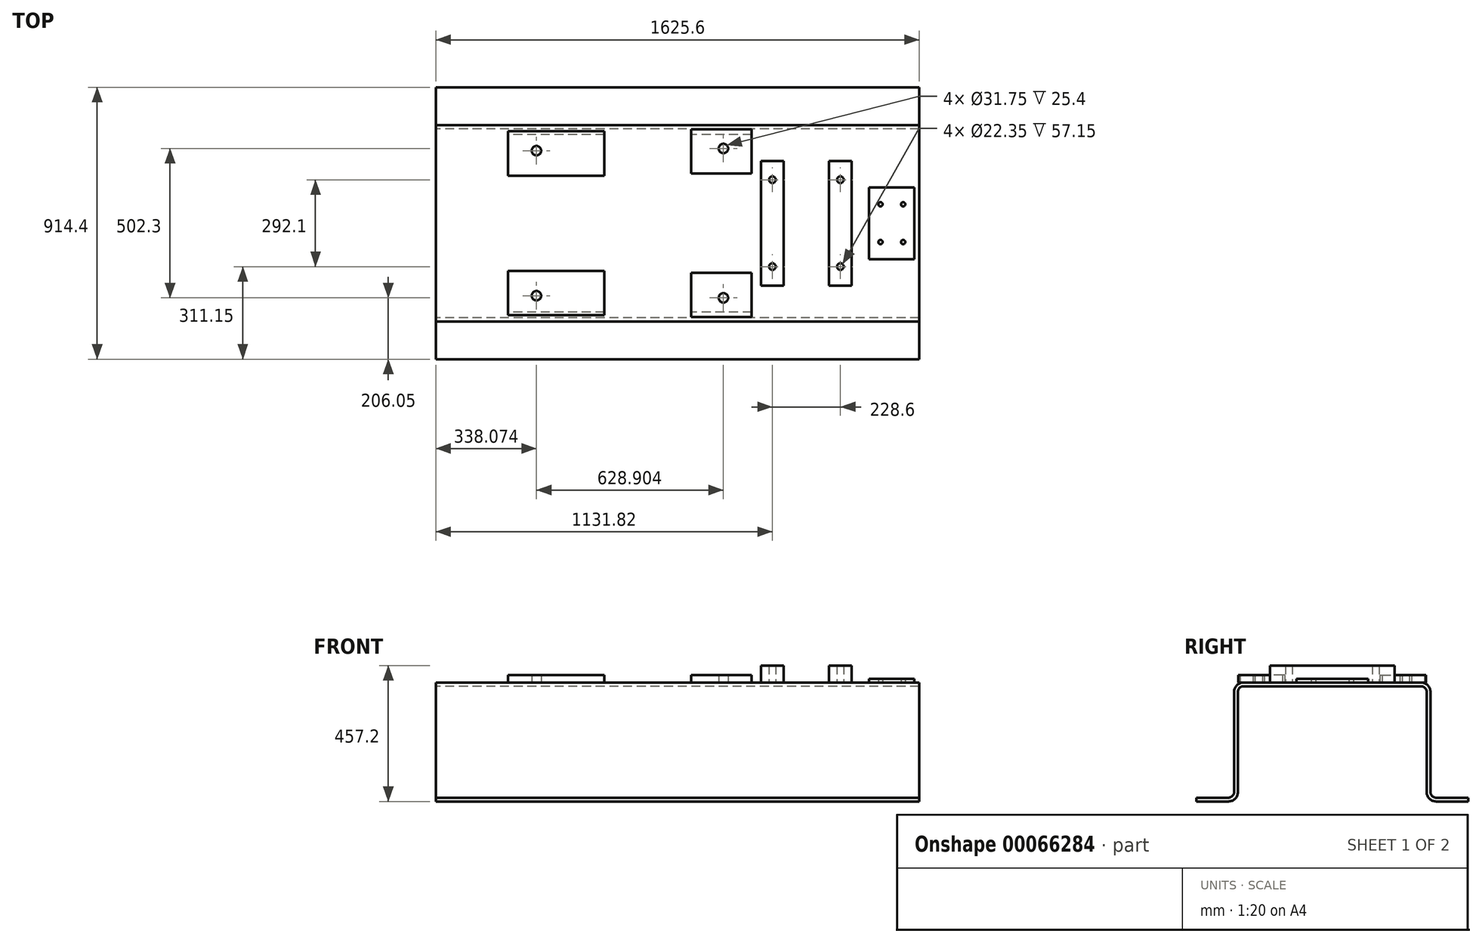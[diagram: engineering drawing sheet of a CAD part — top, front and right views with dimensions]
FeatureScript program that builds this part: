
annotation { "Feature Type Name" : "Feature", "Feature Type Description" : "" }
export const myFeature = defineFeature(function(context is Context, id is Id, definition is map)
    precondition{}
    {
        {
            var Q0;
            Q0=qCreatedBy(makeId("Right.planeOp"),FACE);
            var sketch = newSketch(context, id + "F0", { "sketchPlane" : qUnion([Q0])});
            skLineSegment(sketch, "E0", {"start": v(349.25, 0) * mm, "end": v(457.2, 0) * mm});
            skLineSegment(sketch, "E1.0", {"start": v(349.25, 12.7) * mm, "end": v(457.2, 12.7) * mm});
            skLineSegment(sketch, "E2.0", {"start": v(0, 400.05) * mm, "end": v(298.45, 400.05) * mm});
            skLineSegment(sketch, "E3", {"start": v(0, -167.8) * mm, "end": v(0, 400.05) * mm, "construction": true});
            skLineSegment(sketch, "E4.0", {"start": v(0, 387.35) * mm, "end": v(298.45, 387.35) * mm});
            skLineSegment(sketch, "E5.0", {"start": v(330.2, 31.75) * mm, "end": v(330.2, 368.3) * mm});
            skLineSegment(sketch, "E6.0", {"start": v(317.5, 31.75) * mm, "end": v(317.5, 368.3) * mm});
            skArc(sketch, "E7.filletArc", {"start": v(330.2, 31.75) * mm, "mid": v(335.78, 18.28) * mm, "end": v(349.25, 12.7) * mm});
            skArc(sketch, "E8.filletArc", {"start": v(317.5, 368.3) * mm, "mid": v(311.92, 381.77) * mm, "end": v(298.45, 387.35) * mm});
            skArc(sketch, "E9.filletArc", {"start": v(330.2, 368.3) * mm, "mid": v(320.9, 390.75) * mm, "end": v(298.45, 400.05) * mm});
            skPoint(sketch, "E10.newPointA", {"position": v(-457.2, 0) * mm});
            skArc(sketch, "E10.filletArc", {"start": v(317.5, 31.75) * mm, "mid": v(326.8, 9.3) * mm, "end": v(349.25, 0) * mm});
            skLineSegment(sketch, "E11", {"start": v(457.2, 12.7) * mm, "end": v(457.2, 0) * mm});
            skLineSegment(sketch, "E12.MirrorCS", {"start": v(-457.2, 12.7) * mm, "end": v(-457.2, 0) * mm});
            skArc(sketch, "E13.MirrorCS", {"start": v(-330.2, 368.3) * mm, "mid": v(-320.9, 390.75) * mm, "end": v(-298.45, 400.05) * mm});
            skArc(sketch, "E14.MirrorCS", {"start": v(-330.2, 31.75) * mm, "mid": v(-335.78, 18.28) * mm, "end": v(-349.25, 12.7) * mm});
            skArc(sketch, "E15.MirrorCS", {"start": v(-317.5, 368.3) * mm, "mid": v(-311.92, 381.77) * mm, "end": v(-298.45, 387.35) * mm});
            skArc(sketch, "E16.MirrorCS", {"start": v(-317.5, 31.75) * mm, "mid": v(-326.8, 9.3) * mm, "end": v(-349.25, 0) * mm});
            skLineSegment(sketch, "E17.MirrorCS", {"start": v(-349.25, 0) * mm, "end": v(-457.2, 0) * mm});
            skLineSegment(sketch, "E18.MirrorCS", {"start": v(-349.25, 12.7) * mm, "end": v(-457.2, 12.7) * mm});
            skLineSegment(sketch, "E19.MirrorCS", {"start": v(0, 400.05) * mm, "end": v(-298.45, 400.05) * mm});
            skLineSegment(sketch, "E20.MirrorCS", {"start": v(0, 387.35) * mm, "end": v(-298.45, 387.35) * mm});
            skLineSegment(sketch, "E21.MirrorCS", {"start": v(-317.5, 31.75) * mm, "end": v(-317.5, 368.3) * mm});
            skLineSegment(sketch, "E22.MirrorCS", {"start": v(-330.2, 31.75) * mm, "end": v(-330.2, 368.3) * mm});
            skSolve(sketch);
        }
        {
            var Q0;
            Q0 = qSketchRegion(id + "F0", true);
            extrude(context, id + "F1", {"entities" : qUnion([Q0]), "endBound" : BoundingType.SYMMETRIC, "depth" : 1625.6 * mm});
        }
        {
            var Q0;
            Q0=makeQuery(id+"F1.opExtrude","SWEPT_FACE",FACE,{"disambiguationData":[OSD([sQuery(id+"F0.wireOp",EDGE,"E2.0"),sQuery(id+"F0.wireOp",EDGE,"E19.MirrorCS")])]});
            var sketch = newSketch(context, id + "F2", { "sketchPlane" : qUnion([Q0])});
            skLineSegment(sketch, "E23.0", {"start": v(812.8, -298.45) * mm, "end": v(812.8, 298.45) * mm, "construction": true});
            skLineSegment(sketch, "E24.0", {"start": v(-1600.2, -987.8) * mm, "end": v(-1600.2, 298.45) * mm, "construction": true});
            skLineSegment(sketch, "E25.0", {"start": v(-1143, -987.8) * mm, "end": v(-1143, 298.45) * mm, "construction": true});
            skLineSegment(sketch, "E26.0", {"start": v(-160.27, -987.8) * mm, "end": v(-160.27, 298.45) * mm, "construction": true});
            skLineSegment(sketch, "E27.0", {"start": v(433.32, -987.8) * mm, "end": v(433.32, 298.45) * mm, "construction": true});
            skLineSegment(sketch, "E28.0", {"start": v(45.97, -987.8) * mm, "end": v(45.97, 298.45) * mm, "construction": true});
            skLineSegment(sketch, "E29.0", {"start": v(249.17, -987.8) * mm, "end": v(249.17, 298.45) * mm, "construction": true});
            skLineSegment(sketch, "E30.0", {"start": v(-246.13, -987.8) * mm, "end": v(-246.13, 298.45) * mm, "construction": true});
            skLineSegment(sketch, "E31.0", {"start": v(-569.98, -987.8) * mm, "end": v(-569.98, 298.45) * mm, "construction": true});
            skLineSegment(sketch, "E32.0", {"start": v(-958.44, -155.44) * mm, "end": v(1000.49, -178.16) * mm, "construction": true});
            skLineSegment(sketch, "E33.0", {"start": v(-960.13, -301.48) * mm, "end": v(998.8, -324.2) * mm, "construction": true});
            skLineSegment(sketch, "E34.bottom", {"start": v(-569.98, -159.94) * mm, "end": v(-246.13, -159.94) * mm});
            skLineSegment(sketch, "E34.top", {"start": v(-569.98, -309.76) * mm, "end": v(-246.13, -309.76) * mm});
            skLineSegment(sketch, "E34.left", {"start": v(-569.98, -159.94) * mm, "end": v(-569.98, -309.76) * mm});
            skLineSegment(sketch, "E34.right", {"start": v(-246.13, -159.94) * mm, "end": v(-246.13, -309.76) * mm});
            skLineSegment(sketch, "E35.bottom", {"start": v(45.97, -167.09) * mm, "end": v(249.17, -167.09) * mm});
            skLineSegment(sketch, "E35.top", {"start": v(45.97, -315.5) * mm, "end": v(249.17, -315.5) * mm});
            skLineSegment(sketch, "E35.left", {"start": v(45.97, -167.09) * mm, "end": v(45.97, -315.5) * mm});
            skLineSegment(sketch, "E35.right", {"start": v(249.17, -167.09) * mm, "end": v(249.17, -315.5) * mm});
            skLineSegment(sketch, "E36.0", {"start": v(-474.73, -987.8) * mm, "end": v(-474.73, 298.45) * mm, "construction": true});
            skLineSegment(sketch, "E37.0", {"start": v(154.18, -987.8) * mm, "end": v(154.18, 298.45) * mm, "construction": true});
            skLineSegment(sketch, "E38.0", {"start": v(-959.4, -238.24) * mm, "end": v(999.53, -260.95) * mm, "construction": true});
            skCircle(sketch, "E39", {"center": v(-474.73, -243.86) * mm, "radius": 15.88 * mm});
            skCircle(sketch, "E40", {"center": v(154.18, -251.15) * mm, "radius": 15.88 * mm});
            skLineSegment(sketch, "E41", {"start": v(-969.18, 0) * mm, "end": v(1017.58, 0) * mm, "construction": true});
            skPoint(sketch, "E41.startSnap0", {"position": v(-812.8, 0) * mm});
            skCircle(sketch, "E42.MirrorC", {"center": v(154.18, 251.15) * mm, "radius": 15.88 * mm});
            skCircle(sketch, "E43.MirrorC", {"center": v(-474.73, 243.86) * mm, "radius": 15.88 * mm});
            skLineSegment(sketch, "E44.MirrorCS", {"start": v(-246.13, 159.94) * mm, "end": v(-246.13, 309.76) * mm});
            skLineSegment(sketch, "E45.MirrorCS", {"start": v(45.97, 167.09) * mm, "end": v(249.17, 167.09) * mm});
            skLineSegment(sketch, "E46.MirrorCS", {"start": v(249.17, 167.09) * mm, "end": v(249.17, 315.5) * mm});
            skLineSegment(sketch, "E47.MirrorCS", {"start": v(45.97, 315.5) * mm, "end": v(249.17, 315.5) * mm});
            skLineSegment(sketch, "E48.MirrorCS", {"start": v(-569.98, 159.94) * mm, "end": v(-569.98, 309.76) * mm});
            skLineSegment(sketch, "E49.MirrorCS", {"start": v(-569.98, 309.76) * mm, "end": v(-246.13, 309.76) * mm});
            skLineSegment(sketch, "E50.MirrorCS", {"start": v(45.97, 167.09) * mm, "end": v(45.97, 315.5) * mm});
            skLineSegment(sketch, "E51.MirrorCS", {"start": v(-569.98, 159.94) * mm, "end": v(-246.13, 159.94) * mm});
            skSolve(sketch);
        }
        {
            var Q0;
            Q0 = qSketchRegion(id + "F2", true);
            extrude(context, id + "F3", {"entities" : qUnion([Q0]), "operationType" : NewBodyOperationType.ADD, "depth" : 25.4 * mm});
        }
        {
            var Q0;
            {var subQ7=sQuery(id+"F0.wireOp",EDGE,"E19.MirrorCS");var subQ17=sQuery(id+"F0.wireOp",EDGE,"E9.filletArc");var subQ23=sQuery(id+"F0.wireOp",EDGE,"E2.0");Q0=makeQuery(id+"F3.boolean.opBoolean","SPLIT",FACE,{"disambiguationData":[TD([makeQuery(id+"F1.opExtrude","SWEPT_FACE",FACE,{"disambiguationData":[OSD([subQ17])]})])],"derivedFrom":makeQuery(id+"F1.opExtrude","SWEPT_FACE",FACE,{"disambiguationData":[OSD([subQ23,subQ7])]})});}
            var sketch = newSketch(context, id + "F4", { "sketchPlane" : qUnion([Q0])});
            skLineSegment(sketch, "E52.0", {"start": v(509.52, -209.55) * mm, "end": v(509.52, 209.55) * mm});
            skLineSegment(sketch, "E53.0", {"start": v(585.72, -209.55) * mm, "end": v(585.72, 209.55) * mm});
            skLineSegment(sketch, "E54.0", {"start": v(509.52, 209.55) * mm, "end": v(585.72, 209.55) * mm});
            skLineSegment(sketch, "E55.0", {"start": v(509.52, -209.55) * mm, "end": v(585.72, -209.55) * mm});
            skLineSegment(sketch, "E56.0", {"start": v(547.62, -987.8) * mm, "end": v(547.62, 298.45) * mm, "construction": true});
            skLineSegment(sketch, "E57.0", {"start": v(-969.18, 146.05) * mm, "end": v(1017.58, 146.05) * mm, "construction": true});
            skLineSegment(sketch, "E58.0", {"start": v(-969.18, -146.05) * mm, "end": v(1017.58, -146.05) * mm, "construction": true});
            skCircle(sketch, "E59", {"center": v(547.62, 146.05) * mm, "radius": 11.18 * mm});
            skCircle(sketch, "E60", {"center": v(547.62, -146.05) * mm, "radius": 11.18 * mm});
            skCircle(sketch, "E61.MirrorC", {"center": v(319.02, 146.05) * mm, "radius": 11.18 * mm});
            skCircle(sketch, "E62.MirrorC", {"center": v(319.02, -146.05) * mm, "radius": 11.18 * mm});
            skLineSegment(sketch, "E63.MirrorCS", {"start": v(357.12, -209.55) * mm, "end": v(357.12, 209.55) * mm});
            skLineSegment(sketch, "E64.MirrorCS", {"start": v(280.92, -209.55) * mm, "end": v(280.92, 209.55) * mm});
            skLineSegment(sketch, "E65.MirrorCS", {"start": v(357.12, 209.55) * mm, "end": v(280.92, 209.55) * mm});
            skLineSegment(sketch, "E66.MirrorCS", {"start": v(357.12, -209.55) * mm, "end": v(280.92, -209.55) * mm});
            skSolve(sketch);
        }
        {
            var Q0;
            Q0 = qSketchRegion(id + "F4", true);
            extrude(context, id + "F5", {"entities" : qUnion([Q0]), "operationType" : NewBodyOperationType.ADD, "depth" : 57.15 * mm});
        }
        {
            var Q0;
            {var subQ14=sQuery(id+"F2.wireOp",EDGE,"E34.bottom");Q0=makeQuery(id+"F2.imprint","IMPRINT",FACE,{"disambiguationData":[TD([[makeQuery(id+"F2.imprint","IMPRINT",EDGE,{"derivedFrom":subQ14}),1.0]])]});}
            var sketch = newSketch(context, id + "F6", { "sketchPlane" : qUnion([Q0])});
            skLineSegment(sketch, "E67.0", {"start": v(812.8, -298.45) * mm, "end": v(812.8, 298.45) * mm, "construction": true});
            skLineSegment(sketch, "E68.0", {"start": v(796.8, -298.45) * mm, "end": v(796.8, 298.45) * mm, "construction": true});
            skLineSegment(sketch, "E69.0", {"start": v(644.4, -298.45) * mm, "end": v(644.4, 298.45) * mm, "construction": true});
            skLineSegment(sketch, "E70", {"start": v(0, 0) * mm, "end": v(952.88, 0) * mm, "construction": true});
            skLineSegment(sketch, "E71.0", {"start": v(0, 120.65) * mm, "end": v(952.88, 120.65) * mm, "construction": true});
            skLineSegment(sketch, "E72.0", {"start": v(0, -120.65) * mm, "end": v(952.88, -120.65) * mm, "construction": true});
            skLineSegment(sketch, "E73.bottom", {"start": v(644.4, 120.65) * mm, "end": v(796.8, 120.65) * mm});
            skLineSegment(sketch, "E73.top", {"start": v(644.4, -120.65) * mm, "end": v(796.8, -120.65) * mm});
            skLineSegment(sketch, "E73.left", {"start": v(644.4, 120.65) * mm, "end": v(644.4, -120.65) * mm});
            skLineSegment(sketch, "E73.right", {"start": v(796.8, 120.65) * mm, "end": v(796.8, -120.65) * mm});
            skLineSegment(sketch, "E74.0", {"start": v(0, 63.5) * mm, "end": v(952.88, 63.5) * mm, "construction": true});
            skLineSegment(sketch, "E75.MirrorCS", {"start": v(0, -63.5) * mm, "end": v(952.88, -63.5) * mm, "construction": true});
            skLineSegment(sketch, "E76.0", {"start": v(682.5, -987.8) * mm, "end": v(682.5, 298.45) * mm, "construction": true});
            skLineSegment(sketch, "E77.0", {"start": v(758.7, -987.8) * mm, "end": v(758.7, 298.45) * mm, "construction": true});
            skCircle(sketch, "E78", {"center": v(682.5, 63.5) * mm, "radius": 7.14 * mm});
            skCircle(sketch, "E79", {"center": v(758.7, 63.5) * mm, "radius": 7.14 * mm});
            skCircle(sketch, "E80", {"center": v(682.5, -63.5) * mm, "radius": 7.14 * mm});
            skCircle(sketch, "E81", {"center": v(758.7, -63.5) * mm, "radius": 7.14 * mm});
            skSolve(sketch);
        }
        {
            var Q0;
            Q0 = qSketchRegion(id + "F6", true);
            extrude(context, id + "F7", {"entities" : qUnion([Q0]), "operationType" : NewBodyOperationType.ADD, "depth" : 12.7 * mm});
        }
    });
